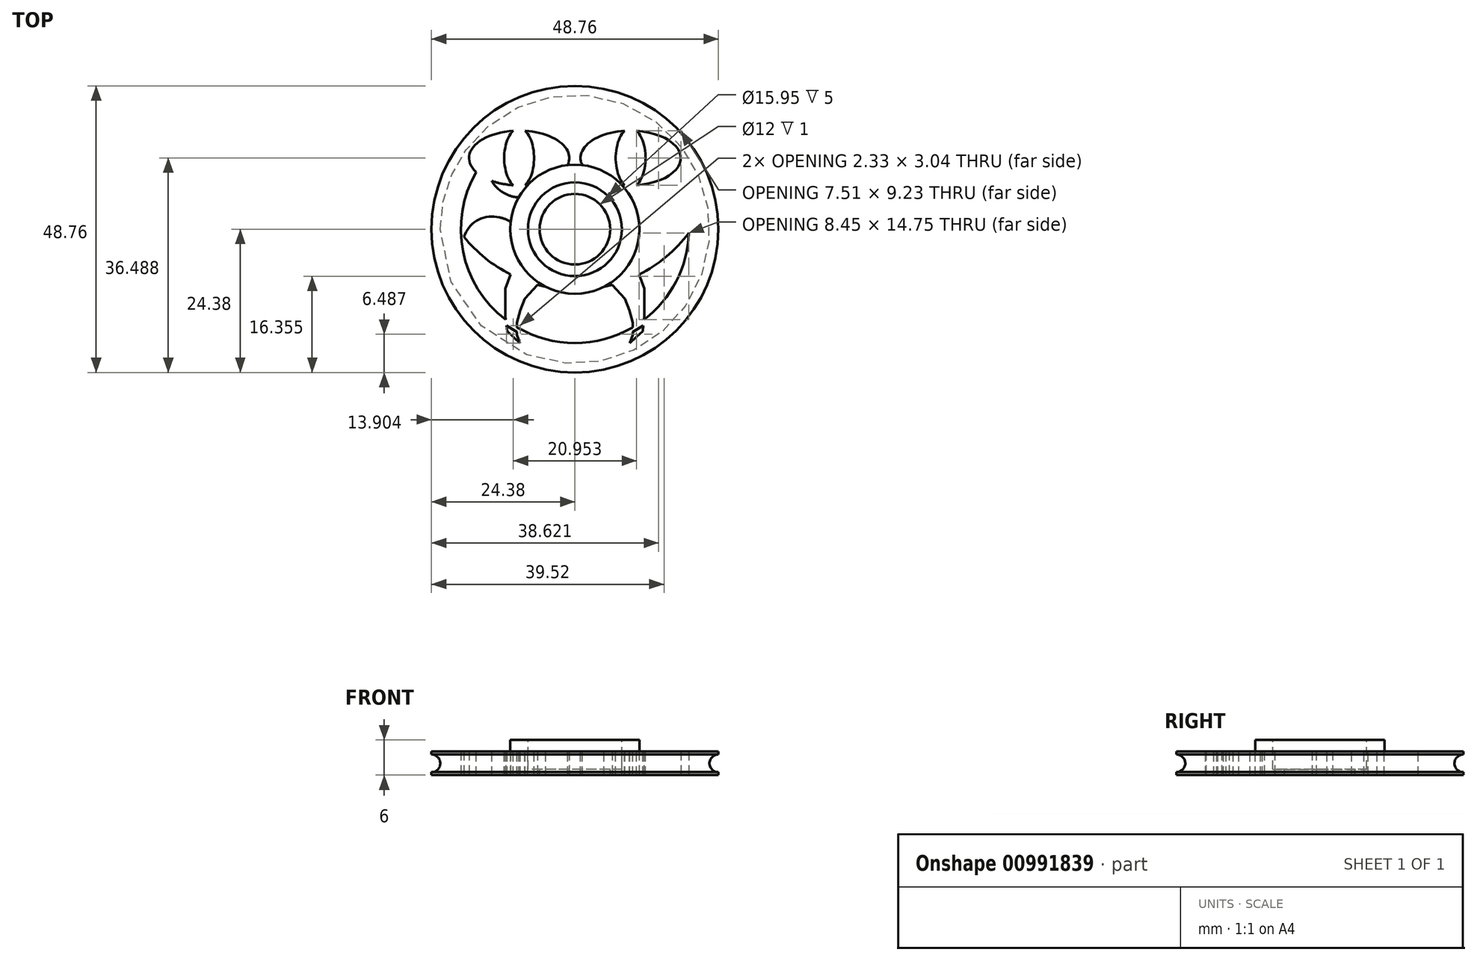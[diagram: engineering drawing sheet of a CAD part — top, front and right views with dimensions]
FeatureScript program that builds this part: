
annotation { "Feature Type Name" : "Feature", "Feature Type Description" : "" }
export const myFeature = defineFeature(function(context is Context, id is Id, definition is map)
    precondition{}
    {
        {
            var Q0;
            Q0=qCreatedBy(makeId("Top.planeOp"),FACE);
            var sketch = newSketch(context, id + "F0", { "sketchPlane" : qUnion([Q0])});
            skCircle(sketch, "E0", {"center": v(0, 0) * mm, "radius": 24.38 * mm});
            skCircle(sketch, "E1", {"center": v(0, 0) * mm, "radius": 8 * mm});
            skArc(sketch, "E2", {"start": v(-4.5, 7.8) * mm, "mid": v(0, -9) * mm, "end": v(4.5, 7.8) * mm});
            skArc(sketch, "E3.0", {"start": v(-9.52, 16.88) * mm, "mid": v(0, -19.38) * mm, "end": v(9.52, 16.88) * mm});
            skLineSegment(sketch, "E4.0", {"start": v(-2.12, 13.29) * mm, "end": v(-2.06, 12.89) * mm});
            skLineSegment(sketch, "E5.0", {"start": v(2.12, 13.29) * mm, "end": v(2.06, 12.89) * mm});
            skPoint(sketch, "E6.orphan", {"position": v(0, 21.65) * mm});
            skPoint(sketch, "E7.visualSharp", {"position": v(-1.44, 8.88) * mm});
            skArc(sketch, "E7.filletArc", {"start": v(-4.5, 7.8) * mm, "mid": v(-2.5, 9.96) * mm, "end": v(-2.06, 12.89) * mm});
            skPoint(sketch, "E8.visualSharp", {"position": v(1.44, 8.88) * mm});
            skArc(sketch, "E8.filletArc", {"start": v(2.06, 12.89) * mm, "mid": v(2.5, 9.96) * mm, "end": v(4.5, 7.8) * mm});
            skPoint(sketch, "E9.visualSharp", {"position": v(3.03, 19.14) * mm});
            skArc(sketch, "E9.filletArc", {"start": v(9.52, 16.88) * mm, "mid": v(4.88, 17.02) * mm, "end": v(2.12, 13.29) * mm});
            skPoint(sketch, "E10.visualSharp", {"position": v(-3.03, 19.14) * mm});
            skArc(sketch, "E10.filletArc", {"start": v(-2.12, 13.29) * mm, "mid": v(-4.88, 17.02) * mm, "end": v(-9.52, 16.88) * mm});
            skArc(sketch, "E11.1.0", {"start": v(-13.3, 2.09) * mm, "mid": v(-17.7, 0.62) * mm, "end": v(-19, -3.84) * mm});
            skLineSegment(sketch, "E11.1.1", {"start": v(-13.3, 2.09) * mm, "end": v(-12.9, 2.02) * mm});
            skArc(sketch, "E11.1.2", {"start": v(-8.8, -1.87) * mm, "mid": v(-10.25, 0.71) * mm, "end": v(-12.9, 2.02) * mm});
            skArc(sketch, "E11.1.3", {"start": v(-11.62, 5.94) * mm, "mid": v(-8.7, 5.45) * mm, "end": v(-6.02, 6.69) * mm});
            skLineSegment(sketch, "E11.1.4", {"start": v(-11.98, 6.12) * mm, "end": v(-11.62, 5.94) * mm});
            skArc(sketch, "E11.1.5", {"start": v(-13.1, 14.27) * mm, "mid": v(-14.68, 9.9) * mm, "end": v(-11.98, 6.12) * mm});
            skArc(sketch, "E11.2.0", {"start": v(-6.1, -12) * mm, "mid": v(-6.06, -16.64) * mm, "end": v(-2.22, -19.25) * mm});
            skLineSegment(sketch, "E11.2.1", {"start": v(-6.1, -12) * mm, "end": v(-5.91, -11.64) * mm});
            skArc(sketch, "E11.2.2", {"start": v(-0.94, -8.95) * mm, "mid": v(-3.84, -9.53) * mm, "end": v(-5.91, -11.64) * mm});
            skArc(sketch, "E11.2.3", {"start": v(-9.24, -9.22) * mm, "mid": v(-7.87, -6.6) * mm, "end": v(-8.22, -3.66) * mm});
            skLineSegment(sketch, "E11.2.4", {"start": v(-9.52, -9.5) * mm, "end": v(-9.24, -9.22) * mm});
            skArc(sketch, "E11.2.5", {"start": v(-17.62, -8.06) * mm, "mid": v(-13.95, -10.9) * mm, "end": v(-9.52, -9.5) * mm});
            skArc(sketch, "E11.3.0", {"start": v(9.52, -9.5) * mm, "mid": v(13.95, -10.9) * mm, "end": v(17.62, -8.06) * mm});
            skLineSegment(sketch, "E11.3.1", {"start": v(9.52, -9.5) * mm, "end": v(9.24, -9.22) * mm});
            skArc(sketch, "E11.3.2", {"start": v(8.22, -3.66) * mm, "mid": v(7.87, -6.6) * mm, "end": v(9.24, -9.22) * mm});
            skArc(sketch, "E11.3.3", {"start": v(5.91, -11.64) * mm, "mid": v(3.84, -9.53) * mm, "end": v(0.94, -8.95) * mm});
            skLineSegment(sketch, "E11.3.4", {"start": v(6.1, -12) * mm, "end": v(5.91, -11.64) * mm});
            skArc(sketch, "E11.3.5", {"start": v(2.22, -19.25) * mm, "mid": v(6.06, -16.64) * mm, "end": v(6.1, -12) * mm});
            skArc(sketch, "E11.4.0", {"start": v(11.98, 6.12) * mm, "mid": v(14.68, 9.9) * mm, "end": v(13.1, 14.27) * mm});
            skLineSegment(sketch, "E11.4.1", {"start": v(11.98, 6.12) * mm, "end": v(11.62, 5.94) * mm});
            skArc(sketch, "E11.4.2", {"start": v(6.02, 6.69) * mm, "mid": v(8.7, 5.45) * mm, "end": v(11.62, 5.94) * mm});
            skArc(sketch, "E11.4.3", {"start": v(12.9, 2.02) * mm, "mid": v(10.25, 0.71) * mm, "end": v(8.8, -1.87) * mm});
            skLineSegment(sketch, "E11.4.4", {"start": v(13.3, 2.09) * mm, "end": v(12.9, 2.02) * mm});
            skArc(sketch, "E11.4.5", {"start": v(19, -3.84) * mm, "mid": v(17.7, 0.62) * mm, "end": v(13.3, 2.09) * mm});
            skCircle(sketch, "E12", {"center": v(0, 13.95) * mm, "radius": 24.25 * mm});
            skSolve(sketch);
        }
        {
            var Q0;
            Q0=makeQuery(id+"F0.imprint","IMPRINT",FACE,{"disambiguationData":[TD([[makeQuery(id+"F0.imprint","IMPRINT",EDGE,{"derivedFrom":sQuery(id+"F0.wireOp",EDGE,"E0")}),1.0]])]});
            var Q1;
            {var subQ0=sQuery(id+"F0.wireOp",EDGE,"E11.4.0");Q1=makeQuery(id+"F0.imprint","IMPRINT",FACE,{"disambiguationData":[TD([[makeQuery(id+"F0.imprint","IMPRINT",EDGE,{"derivedFrom":subQ0}),-1.0]])]});}
            var Q2;
            Q2=makeQuery(id+"F0.imprint","IMPRINT",FACE,{"disambiguationData":[TD([[makeQuery(id+"F0.imprint","IMPRINT",EDGE,{"derivedFrom":sQuery(id+"F0.wireOp",EDGE,"E1")}),-1.0]])]});
            var Q3;
            {var subQ0=sQuery(id+"F0.wireOp",EDGE,"E11.1.1");Q3=makeQuery(id+"F0.imprint","IMPRINT",FACE,{"disambiguationData":[TD([[makeQuery(id+"F0.imprint","IMPRINT",EDGE,{"derivedFrom":subQ0}),1.0]])]});}
            var Q4;
            {var subQ1=sQuery(id+"F0.wireOp",EDGE,"E11.2.3");Q4=makeQuery(id+"F0.imprint","IMPRINT",FACE,{"disambiguationData":[TD([[makeQuery(id+"F0.imprint","IMPRINT",EDGE,{"derivedFrom":subQ1}),-1.0]])]});}
            var Q5;
            {var subQ5=sQuery(id+"F0.wireOp",EDGE,"E11.3.2");Q5=makeQuery(id+"F0.imprint","IMPRINT",FACE,{"disambiguationData":[TD([[makeQuery(id+"F0.imprint","IMPRINT",EDGE,{"derivedFrom":subQ5}),-1.0]])]});}
            var Q6;
            {var subQ1=sQuery(id+"F0.wireOp",EDGE,"E11.1.1");Q6=makeQuery(id+"F0.imprint","IMPRINT",FACE,{"disambiguationData":[TD([[makeQuery(id+"F0.imprint","IMPRINT",EDGE,{"derivedFrom":subQ1}),-1.0]])]});}
            var Q7;
            {var subQ0=sQuery(id+"F0.wireOp",EDGE,"E11.2.2");var subQ1=sQuery(id+"F0.wireOp",EDGE,"E2");var subQ2=makeQuery(id+"F0.imprint","INTERSECT",VERTEX,{"derivedFrom":[subQ1,subQ0]});Q7=makeQuery(id+"F0.imprint","IMPRINT",FACE,{"disambiguationData":[TD([[makeQuery(id+"F0.imprint","IMPRINT",EDGE,{"disambiguationData":[TD([[subQ2,-1.0]])],"derivedFrom":subQ1}),-1.0]])]});}
            var Q8;
            {var subQ0=sQuery(id+"F0.wireOp",EDGE,"E11.4.3");Q8=makeQuery(id+"F0.imprint","IMPRINT",FACE,{"disambiguationData":[TD([[makeQuery(id+"F0.imprint","IMPRINT",EDGE,{"derivedFrom":subQ0}),1.0]])]});}
            extrude(context, id + "F1", {"entities" : qUnion([Q0, Q1, Q2, Q3, Q4, Q5, Q6, Q7, Q8]), "depth" : 4 * mm, "offsetDistance" : 25.4 * mm, "symmetric" : true});
        }
        {
            var Q0;
            Q0=qCreatedBy(makeId("Top.planeOp"),FACE);
            var sketch = newSketch(context, id + "F2", { "sketchPlane" : qUnion([Q0])});
            skLineSegment(sketch, "E13", {"start": v(-14.44, -5.48) * mm, "end": v(-16.84, -9.61) * mm});
            skLineSegment(sketch, "E14", {"start": v(-16.84, -9.61) * mm, "end": v(-15.72, -11.69) * mm});
            skLineSegment(sketch, "E15", {"start": v(-15.72, -11.69) * mm, "end": v(-12.24, -6.68) * mm});
            skLineSegment(sketch, "E16", {"start": v(-12.24, -6.68) * mm, "end": v(-9.08, -8.27) * mm});
            skLineSegment(sketch, "E17", {"start": v(-9.08, -8.27) * mm, "end": v(-12.78, -12.6) * mm});
            skLineSegment(sketch, "E18", {"start": v(-12.78, -12.6) * mm, "end": v(-13.23, -11.08) * mm});
            skLineSegment(sketch, "E19", {"start": v(-13.23, -11.08) * mm, "end": v(-14.16, -11.08) * mm});
            skLineSegment(sketch, "E20", {"start": v(-14.16, -11.08) * mm, "end": v(-14.82, -11.08) * mm});
            skLineSegment(sketch, "E21", {"start": v(-14.82, -11.08) * mm, "end": v(-15.14, -10.86) * mm});
            skLineSegment(sketch, "E22", {"start": v(-4.98, -9.03) * mm, "end": v(-8.45, -15.68) * mm});
            skLineSegment(sketch, "E23", {"start": v(-1.8, -17.1) * mm, "end": v(-0.72, -9.57) * mm});
            skLineSegment(sketch, "E24", {"start": v(0.8, -9.78) * mm, "end": v(1.77, -17.83) * mm});
            skLineSegment(sketch, "E25", {"start": v(6.47, -15.97) * mm, "end": v(4.75, -8.64) * mm});
            skLineSegment(sketch, "E26", {"start": v(-8.6, -8.27) * mm, "end": v(-13.47, -13.99) * mm});
            skLineSegment(sketch, "E27", {"start": v(-13.47, -13.99) * mm, "end": v(-12.24, -13.99) * mm});
            skLineSegment(sketch, "E28", {"start": v(-12.24, -13.99) * mm, "end": v(-11.5, -14.36) * mm});
            skLineSegment(sketch, "E29", {"start": v(-11.5, -14.36) * mm, "end": v(-11.43, -15.48) * mm});
            skLineSegment(sketch, "E30", {"start": v(-11.43, -15.48) * mm, "end": v(-11, -16.02) * mm});
            skLineSegment(sketch, "E31", {"start": v(-11, -16.02) * mm, "end": v(-10.2, -16.27) * mm});
            skLineSegment(sketch, "E32", {"start": v(-10.2, -16.27) * mm, "end": v(-7.92, -13.58) * mm});
            skLineSegment(sketch, "E33", {"start": v(-7.92, -13.58) * mm, "end": v(-6.92, -11.6) * mm});
            skLineSegment(sketch, "E34", {"start": v(-6.92, -11.6) * mm, "end": v(-6.1, -8.93) * mm});
            skLineSegment(sketch, "E35", {"start": v(5.83, -9.57) * mm, "end": v(6.89, -14.1) * mm});
            skLineSegment(sketch, "E36", {"start": v(6.89, -14.1) * mm, "end": v(11.16, -12.01) * mm});
            skLineSegment(sketch, "E37", {"start": v(11.16, -12.01) * mm, "end": v(10.22, -7.97) * mm});
            skLineSegment(sketch, "E38", {"start": v(10.22, -7.97) * mm, "end": v(13.16, -14.55) * mm});
            skLineSegment(sketch, "E39", {"start": v(13.16, -14.55) * mm, "end": v(14.29, -13.09) * mm});
            skLineSegment(sketch, "E40", {"start": v(14.29, -13.09) * mm, "end": v(15.36, -10.64) * mm});
            skLineSegment(sketch, "E41", {"start": v(15.36, -10.64) * mm, "end": v(14.11, -10.46) * mm});
            skLineSegment(sketch, "E42", {"start": v(14.11, -10.46) * mm, "end": v(13.16, -9.57) * mm});
            skLineSegment(sketch, "E43", {"start": v(13.16, -9.57) * mm, "end": v(13.16, -7.95) * mm});
            skLineSegment(sketch, "E44", {"start": v(13.16, -7.95) * mm, "end": v(13.02, -6.39) * mm});
            skLineSegment(sketch, "E45", {"start": v(-14.44, -5.48) * mm, "end": v(-12.24, -6.68) * mm});
            skLineSegment(sketch, "E46", {"start": v(-8.6, -8.27) * mm, "end": v(-6.1, -8.93) * mm});
            skLineSegment(sketch, "E47", {"start": v(-4.98, -9.03) * mm, "end": v(-0.72, -9.57) * mm});
            skLineSegment(sketch, "E48", {"start": v(0.8, -9.78) * mm, "end": v(4.75, -8.64) * mm});
            skLineSegment(sketch, "E49", {"start": v(5.83, -9.57) * mm, "end": v(10.22, -7.97) * mm});
            skLineSegment(sketch, "E50", {"start": v(10.22, -7.97) * mm, "end": v(13.02, -6.39) * mm});
            skLineSegment(sketch, "E51", {"start": v(13.52, -5.97) * mm, "end": v(14.5, -8.94) * mm});
            skLineSegment(sketch, "E52", {"start": v(14.5, -8.94) * mm, "end": v(15.67, -8.94) * mm});
            skLineSegment(sketch, "E53", {"start": v(15.67, -8.94) * mm, "end": v(16.95, -8.28) * mm});
            skLineSegment(sketch, "E54", {"start": v(16.95, -8.28) * mm, "end": v(17.81, -7.9) * mm});
            skLineSegment(sketch, "E55", {"start": v(17.81, -7.9) * mm, "end": v(18.02, -7.07) * mm});
            skLineSegment(sketch, "E56", {"start": v(18.02, -7.07) * mm, "end": v(17.67, -6.3) * mm});
            skLineSegment(sketch, "E57", {"start": v(17.67, -6.3) * mm, "end": v(17.06, -4.94) * mm});
            skLineSegment(sketch, "E58", {"start": v(17.06, -4.94) * mm, "end": v(16.19, -3.72) * mm});
            skLineSegment(sketch, "E59", {"start": v(16.19, -3.72) * mm, "end": v(13.52, -5.97) * mm});
            skLineSegment(sketch, "E60", {"start": v(-8.45, -15.68) * mm, "end": v(-6.08, -16.91) * mm});
            skLineSegment(sketch, "E61", {"start": v(-6.08, -16.91) * mm, "end": v(-4.84, -18.74) * mm});
            skLineSegment(sketch, "E62", {"start": v(-4.84, -18.74) * mm, "end": v(-3.33, -19.9) * mm});
            skLineSegment(sketch, "E63", {"start": v(-3.33, -19.9) * mm, "end": v(-1.8, -17.1) * mm});
            skLineSegment(sketch, "E64", {"start": v(11.16, -12.01) * mm, "end": v(11.88, -11.69) * mm});
            skLineSegment(sketch, "E65", {"start": v(1.77, -17.83) * mm, "end": v(3.1, -17.67) * mm});
            skLineSegment(sketch, "E66", {"start": v(3.1, -17.67) * mm, "end": v(3.94, -18.9) * mm});
            skLineSegment(sketch, "E67", {"start": v(3.94, -18.9) * mm, "end": v(5.39, -18.9) * mm});
            skLineSegment(sketch, "E68", {"start": v(5.39, -18.9) * mm, "end": v(5.39, -17.83) * mm});
            skLineSegment(sketch, "E69", {"start": v(5.84, -13.31) * mm, "end": v(6.47, -15.97) * mm});
            skLineSegment(sketch, "E70", {"start": v(5.39, -17.83) * mm, "end": v(6.5, -17.3) * mm});
            skLineSegment(sketch, "E71", {"start": v(6.5, -17.3) * mm, "end": v(6.47, -15.97) * mm});
            skSolve(sketch);
        }
        {
            var Q0;
            Q0=qCreatedBy(makeId("Top.planeOp"),FACE);
            var sketch = newSketch(context, id + "F3", { "sketchPlane" : qUnion([Q0])});
            skEllipse(sketch, "E72", {"center": v(-9.48, 12.1) * mm, "majorRadius": 8.52 * mm, "minorRadius": 4.65 * mm, "majorAxis": v(-1, 0)});
            skEllipse(sketch, "E73.MirrorC", {"center": v(9.48, 12.1) * mm, "majorRadius": 8.52 * mm, "minorRadius": 4.65 * mm, "majorAxis": v(1, 0)});
            skSolve(sketch);
        }
        {
            var Q0;
            Q0=makeQuery(id+"F0.imprint","IMPRINT",FACE,{"disambiguationData":[TD([[makeQuery(id+"F0.imprint","IMPRINT",EDGE,{"derivedFrom":sQuery(id+"F0.wireOp",EDGE,"E1")}),-1.0]])]});
            var Q1;
            {var subQ0=sQuery(id+"F0.wireOp",EDGE,"E11.1.1");Q1=makeQuery(id+"F0.imprint","IMPRINT",FACE,{"disambiguationData":[TD([[makeQuery(id+"F0.imprint","IMPRINT",EDGE,{"derivedFrom":subQ0}),1.0]])]});}
            var Q2;
            {var subQ0=sQuery(id+"F0.wireOp",EDGE,"E11.4.0");Q2=makeQuery(id+"F0.imprint","IMPRINT",FACE,{"disambiguationData":[TD([[makeQuery(id+"F0.imprint","IMPRINT",EDGE,{"derivedFrom":subQ0}),-1.0]])]});}
            var Q3;
            Q3=makeQuery(id+"F0.imprint","IMPRINT",FACE,{"disambiguationData":[TD([[makeQuery(id+"F0.imprint","IMPRINT",EDGE,{"derivedFrom":sQuery(id+"F0.wireOp",EDGE,"E5.0")}),1.0]])]});
            var Q4;
            Q4=makeQuery(id+"F0.imprint","IMPRINT",FACE,{"disambiguationData":[TD([[makeQuery(id+"F0.imprint","IMPRINT",EDGE,{"derivedFrom":sQuery(id+"F0.wireOp",EDGE,"E4.0")}),-1.0]])]});
            extrude(context, id + "F4", {"entities" : qUnion([Q0, Q1, Q2, Q3, Q4]), "operationType" : NewBodyOperationType.ADD, "depth" : 4 * mm, "offsetDistance" : 25.4 * mm, "symmetric" : true});
        }
        {
            var Q0;
            Q0=qSketchRegion(id+"F3",true);
            extrude(context, id + "F5", {"entities" : qUnion([Q0]), "operationType" : NewBodyOperationType.REMOVE, "oppositeDirection" : true, "depth" : 5 * mm, "offsetDistance" : 25.4 * mm, "symmetric" : true});
        }
        {
            var Q0;
            {var subQ0=sQuery(id+"F0.wireOp",EDGE,"E12");var subQ1=sQuery(id+"F0.wireOp",EDGE,"E11.1.0");var subQ2=sQuery(id+"F0.wireOp",EDGE,"E2");var subQ3=sQuery(id+"F0.wireOp",EDGE,"E1");var subQ4=sQuery(id+"F0.wireOp",EDGE,"E0");Q0=makeQuery(id+"F4.boolean.opBoolean","MERGE",FACE,{"derivedFrom":[makeQuery(id+"F1.opExtrude","CAP_FACE",FACE,{"disambiguationData":[OSD([subQ4,subQ3,subQ2,sQuery(id+"F0.wireOp",EDGE,"E3.0"),sQuery(id+"F0.wireOp",EDGE,"E4.0"),sQuery(id+"F0.wireOp",EDGE,"E5.0"),sQuery(id+"F0.wireOp",EDGE,"E7.filletArc"),sQuery(id+"F0.wireOp",EDGE,"E8.filletArc"),sQuery(id+"F0.wireOp",EDGE,"E9.filletArc"),sQuery(id+"F0.wireOp",EDGE,"E10.filletArc"),subQ1,sQuery(id+"F0.wireOp",EDGE,"E11.1.3"),sQuery(id+"F0.wireOp",EDGE,"E11.1.4"),sQuery(id+"F0.wireOp",EDGE,"E11.1.5"),sQuery(id+"F0.wireOp",EDGE,"E11.4.0"),sQuery(id+"F0.wireOp",EDGE,"E11.4.1"),sQuery(id+"F0.wireOp",EDGE,"E11.4.2"),subQ0])],"isStart":false}),makeQuery(id+"F4.opExtrude","CAP_FACE",FACE,{"disambiguationData":[OSD([subQ4,subQ3,subQ2,subQ1,sQuery(id+"F0.wireOp",EDGE,"E11.1.1"),sQuery(id+"F0.wireOp",EDGE,"E11.1.2"),sQuery(id+"F0.wireOp",EDGE,"E11.4.3"),sQuery(id+"F0.wireOp",EDGE,"E11.4.4"),sQuery(id+"F0.wireOp",EDGE,"E11.4.5"),subQ0])],"isStart":false})]});}
            var sketch = newSketch(context, id + "F6", { "sketchPlane" : qUnion([Q0])});
            skLineSegment(sketch, "E74", {"start": v(-10.73, -7.2) * mm, "end": v(-11.83, -10.11) * mm});
            skLineSegment(sketch, "E75", {"start": v(-11.83, -10.11) * mm, "end": v(-11.83, -13.22) * mm});
            skLineSegment(sketch, "E76", {"start": v(-11.83, -13.22) * mm, "end": v(-11.83, -14.74) * mm});
            skLineSegment(sketch, "E77", {"start": v(-11.83, -14.74) * mm, "end": v(-11.21, -16.75) * mm});
            skLineSegment(sketch, "E78", {"start": v(-11.21, -16.75) * mm, "end": v(-9.83, -18) * mm});
            skLineSegment(sketch, "E79", {"start": v(-9.83, -18) * mm, "end": v(-9.83, -15.92) * mm});
            skLineSegment(sketch, "E80", {"start": v(-9.83, -15.92) * mm, "end": v(-9.28, -13.78) * mm});
            skLineSegment(sketch, "E81", {"start": v(-9.28, -13.78) * mm, "end": v(-8.51, -11.84) * mm});
            skLineSegment(sketch, "E82", {"start": v(-8.51, -11.84) * mm, "end": v(-7.06, -10.22) * mm});
            skLineSegment(sketch, "E83", {"start": v(-7.06, -10.22) * mm, "end": v(-6.26, -9.33) * mm});
            skLineSegment(sketch, "E84", {"start": v(-6.26, -9.33) * mm, "end": v(-5.61, -7.98) * mm});
            skLineSegment(sketch, "E85", {"start": v(-5.61, -7.98) * mm, "end": v(-9.83, -5.47) * mm});
            skLineSegment(sketch, "E86", {"start": v(-9.83, -5.47) * mm, "end": v(-10.73, -7.2) * mm});
            skLineSegment(sketch, "E87", {"start": v(-11.83, -14.74) * mm, "end": v(-11.52, -17.36) * mm});
            skPoint(sketch, "E87.endSnap0", {"position": v(-11.52, -15.75) * mm});
            skLineSegment(sketch, "E88", {"start": v(-11.52, -17.36) * mm, "end": v(-10.42, -18.39) * mm});
            skLineSegment(sketch, "E89", {"start": v(-10.42, -18.39) * mm, "end": v(-9.31, -19.41) * mm});
            skLineSegment(sketch, "E90", {"start": v(-9.31, -19.41) * mm, "end": v(-9.83, -18) * mm});
            skLineSegment(sketch, "E91", {"start": v(-9.83, -17.52) * mm, "end": v(-11.6, -16.66) * mm});
            skLineSegment(sketch, "E92", {"start": v(-9.83, -16.96) * mm, "end": v(-11.71, -15.78) * mm});
            skLineSegment(sketch, "E93.MirrorCS", {"start": v(5.61, -7.98) * mm, "end": v(9.83, -5.47) * mm});
            skLineSegment(sketch, "E94.MirrorCS", {"start": v(9.83, -5.47) * mm, "end": v(10.73, -7.2) * mm});
            skLineSegment(sketch, "E95.MirrorCS", {"start": v(10.73, -7.2) * mm, "end": v(11.83, -10.11) * mm});
            skLineSegment(sketch, "E96.MirrorCS", {"start": v(11.83, -10.11) * mm, "end": v(11.83, -13.22) * mm});
            skLineSegment(sketch, "E97.MirrorCS", {"start": v(11.83, -13.22) * mm, "end": v(11.83, -14.74) * mm});
            skLineSegment(sketch, "E98.MirrorCS", {"start": v(11.83, -14.74) * mm, "end": v(11.52, -17.36) * mm});
            skLineSegment(sketch, "E99.MirrorCS", {"start": v(11.52, -17.36) * mm, "end": v(10.42, -18.39) * mm});
            skLineSegment(sketch, "E100.MirrorCS", {"start": v(10.42, -18.39) * mm, "end": v(9.31, -19.41) * mm});
            skLineSegment(sketch, "E101.MirrorCS", {"start": v(9.31, -19.41) * mm, "end": v(9.83, -18) * mm});
            skLineSegment(sketch, "E102.MirrorCS", {"start": v(9.83, -15.92) * mm, "end": v(9.28, -13.78) * mm});
            skLineSegment(sketch, "E103.MirrorCS", {"start": v(9.28, -13.78) * mm, "end": v(8.51, -11.84) * mm});
            skLineSegment(sketch, "E104.MirrorCS", {"start": v(8.51, -11.84) * mm, "end": v(7.06, -10.22) * mm});
            skLineSegment(sketch, "E105.MirrorCS", {"start": v(7.06, -10.22) * mm, "end": v(6.26, -9.33) * mm});
            skLineSegment(sketch, "E106.MirrorCS", {"start": v(6.26, -9.33) * mm, "end": v(5.61, -7.98) * mm});
            skLineSegment(sketch, "E107.MirrorCS", {"start": v(9.83, -18) * mm, "end": v(9.83, -15.92) * mm});
            skLineSegment(sketch, "E108.MirrorCS", {"start": v(9.83, -16.96) * mm, "end": v(11.71, -15.78) * mm});
            skLineSegment(sketch, "E109.MirrorCS", {"start": v(11.21, -16.75) * mm, "end": v(9.83, -18) * mm});
            skLineSegment(sketch, "E110.MirrorCS", {"start": v(9.83, -17.52) * mm, "end": v(11.6, -16.66) * mm});
            skSolve(sketch);
        }
        {
            var Q0;
            Q0=qSketchRegion(id+"F6",true);
            extrude(context, id + "F7", {"entities" : qUnion([Q0]), "operationType" : NewBodyOperationType.ADD, "oppositeDirection" : true, "depth" : 4 * mm, "offsetDistance" : 25.4 * mm});
        }
        {
            var Q0;
            {var subQ3=sQuery(id+"F6.wireOp",EDGE,"E78");var subQ5=sQuery(id+"F6.wireOp",EDGE,"E77");var subQ6=makeQuery(id+"F6.imprint","INTERSECT",VERTEX,{"derivedFrom":[subQ5,subQ3]});Q0=makeQuery(id+"F6.imprint","IMPRINT",FACE,{"disambiguationData":[TD([[makeQuery(id+"F6.imprint","IMPRINT",EDGE,{"disambiguationData":[TD([[subQ6,1.0]])],"derivedFrom":subQ5}),-1.0]])]});}
            var Q1;
            {var subQ3=sQuery(id+"F6.wireOp",EDGE,"E78");var subQ5=sQuery(id+"F6.wireOp",EDGE,"E77");var subQ6=makeQuery(id+"F6.imprint","INTERSECT",VERTEX,{"derivedFrom":[subQ5,subQ3]});Q1=makeQuery(id+"F6.imprint","IMPRINT",FACE,{"disambiguationData":[TD([[makeQuery(id+"F6.imprint","IMPRINT",EDGE,{"disambiguationData":[TD([[subQ6,1.0]])],"derivedFrom":subQ5}),1.0]])]});}
            var Q2;
            {var subQ0=sQuery(id+"F6.wireOp",EDGE,"E79");var subQ3=sQuery(id+"F6.wireOp",EDGE,"E91");var subQ5=makeQuery(id+"F6.imprint","INTERSECT",VERTEX,{"derivedFrom":[subQ0,subQ3]});Q2=makeQuery(id+"F6.imprint","IMPRINT",FACE,{"disambiguationData":[TD([[makeQuery(id+"F6.imprint","IMPRINT",EDGE,{"disambiguationData":[TD([[subQ5,-1.0]])],"derivedFrom":subQ3}),1.0]])]});}
            var Q3;
            {var subQ0=sQuery(id+"F6.wireOp",EDGE,"E88");Q3=makeQuery(id+"F6.imprint","IMPRINT",FACE,{"disambiguationData":[TD([[makeQuery(id+"F6.imprint","IMPRINT",EDGE,{"derivedFrom":subQ0}),1.0]])]});}
            var Q4;
            {var subQ1=sQuery(id+"F6.wireOp",EDGE,"E107.MirrorCS");var subQ3=sQuery(id+"F6.wireOp",EDGE,"E110.MirrorCS");var subQ4=makeQuery(id+"F6.imprint","INTERSECT",VERTEX,{"derivedFrom":[subQ1,subQ3]});Q4=makeQuery(id+"F6.imprint","IMPRINT",FACE,{"disambiguationData":[TD([[makeQuery(id+"F6.imprint","IMPRINT",EDGE,{"disambiguationData":[TD([[subQ4,-1.0]])],"derivedFrom":subQ3}),-1.0]])]});}
            var Q5;
            {var subQ1=sQuery(id+"F6.wireOp",EDGE,"E99.MirrorCS");Q5=makeQuery(id+"F6.imprint","IMPRINT",FACE,{"disambiguationData":[TD([[makeQuery(id+"F6.imprint","IMPRINT",EDGE,{"derivedFrom":subQ1}),-1.0]])]});}
            var Q6;
            {var subQ4=sQuery(id+"F6.wireOp",EDGE,"E108.MirrorCS");Q6=makeQuery(id+"F6.imprint","IMPRINT",FACE,{"disambiguationData":[TD([[makeQuery(id+"F6.imprint","IMPRINT",EDGE,{"derivedFrom":subQ4}),-1.0]])]});}
            extrude(context, id + "F8", {"entities" : qUnion([Q0, Q1, Q2, Q3, Q4, Q5, Q6]), "operationType" : NewBodyOperationType.REMOVE, "oppositeDirection" : true, "depth" : 25.4 * mm, "offsetDistance" : 25.4 * mm});
        }
        {
            var Q0;
            Q0=qCreatedBy(makeId("Front.planeOp"),FACE);
            var sketch = newSketch(context, id + "F9", { "sketchPlane" : qUnion([Q0])});
            skCircle(sketch, "E111", {"center": v(-24.38, 0) * mm, "radius": 1.5 * mm});
            skLineSegment(sketch, "E112", {"start": v(0, 3.3) * mm, "end": v(0, -4.33) * mm, "construction": true});
            skSolve(sketch);
        }
        {
            var Q0;
            {var subQ0=sQuery(id+"F0.wireOp",EDGE,"E12");var subQ1=sQuery(id+"F0.wireOp",EDGE,"E11.1.0");var subQ2=sQuery(id+"F0.wireOp",EDGE,"E2");var subQ3=sQuery(id+"F0.wireOp",EDGE,"E1");var subQ4=sQuery(id+"F0.wireOp",EDGE,"E0");Q0=makeQuery(id+"F7.boolean.opBoolean","MERGE",FACE,{"derivedFrom":[makeQuery(id+"F4.boolean.opBoolean","MERGE",FACE,{"derivedFrom":[makeQuery(id+"F1.opExtrude","CAP_FACE",FACE,{"disambiguationData":[OSD([subQ4,subQ3,subQ2,sQuery(id+"F0.wireOp",EDGE,"E3.0"),sQuery(id+"F0.wireOp",EDGE,"E4.0"),sQuery(id+"F0.wireOp",EDGE,"E5.0"),sQuery(id+"F0.wireOp",EDGE,"E7.filletArc"),sQuery(id+"F0.wireOp",EDGE,"E8.filletArc"),sQuery(id+"F0.wireOp",EDGE,"E9.filletArc"),sQuery(id+"F0.wireOp",EDGE,"E10.filletArc"),subQ1,sQuery(id+"F0.wireOp",EDGE,"E11.1.3"),sQuery(id+"F0.wireOp",EDGE,"E11.1.4"),sQuery(id+"F0.wireOp",EDGE,"E11.1.5"),sQuery(id+"F0.wireOp",EDGE,"E11.4.0"),sQuery(id+"F0.wireOp",EDGE,"E11.4.1"),sQuery(id+"F0.wireOp",EDGE,"E11.4.2"),subQ0])],"isStart":false}),makeQuery(id+"F4.opExtrude","CAP_FACE",FACE,{"disambiguationData":[OSD([subQ4,subQ3,subQ2,subQ1,sQuery(id+"F0.wireOp",EDGE,"E11.1.1"),sQuery(id+"F0.wireOp",EDGE,"E11.1.2"),sQuery(id+"F0.wireOp",EDGE,"E11.4.3"),sQuery(id+"F0.wireOp",EDGE,"E11.4.4"),sQuery(id+"F0.wireOp",EDGE,"E11.4.5"),subQ0])],"isStart":false})]}),makeQuery(id+"F7.opExtrude","CAP_FACE",FACE,{"disambiguationData":[OSD([sQuery(id+"F6.wireOp",EDGE,"E74"),sQuery(id+"F6.wireOp",EDGE,"E75"),sQuery(id+"F6.wireOp",EDGE,"E76"),sQuery(id+"F6.wireOp",EDGE,"E79"),sQuery(id+"F6.wireOp",EDGE,"E80"),sQuery(id+"F6.wireOp",EDGE,"E81"),sQuery(id+"F6.wireOp",EDGE,"E82"),sQuery(id+"F6.wireOp",EDGE,"E83"),sQuery(id+"F6.wireOp",EDGE,"E84"),sQuery(id+"F6.wireOp",EDGE,"E85"),sQuery(id+"F6.wireOp",EDGE,"E86"),sQuery(id+"F6.wireOp",EDGE,"E87"),sQuery(id+"F6.wireOp",EDGE,"E88"),sQuery(id+"F6.wireOp",EDGE,"E89"),sQuery(id+"F6.wireOp",EDGE,"E90")])],"isStart":true}),makeQuery(id+"F7.opExtrude","CAP_FACE",FACE,{"disambiguationData":[OSD([sQuery(id+"F6.wireOp",EDGE,"E93.MirrorCS"),sQuery(id+"F6.wireOp",EDGE,"E94.MirrorCS"),sQuery(id+"F6.wireOp",EDGE,"E95.MirrorCS"),sQuery(id+"F6.wireOp",EDGE,"E96.MirrorCS"),sQuery(id+"F6.wireOp",EDGE,"E97.MirrorCS"),sQuery(id+"F6.wireOp",EDGE,"E98.MirrorCS"),sQuery(id+"F6.wireOp",EDGE,"E99.MirrorCS"),sQuery(id+"F6.wireOp",EDGE,"E100.MirrorCS"),sQuery(id+"F6.wireOp",EDGE,"E101.MirrorCS"),sQuery(id+"F6.wireOp",EDGE,"E102.MirrorCS"),sQuery(id+"F6.wireOp",EDGE,"E103.MirrorCS"),sQuery(id+"F6.wireOp",EDGE,"E104.MirrorCS"),sQuery(id+"F6.wireOp",EDGE,"E105.MirrorCS"),sQuery(id+"F6.wireOp",EDGE,"E106.MirrorCS"),sQuery(id+"F6.wireOp",EDGE,"E107.MirrorCS")])],"isStart":true})]});}
            var sketch = newSketch(context, id + "F10", { "sketchPlane" : qUnion([Q0])});
            skEllipse(sketch, "E113", {"center": v(-9.48, 12.1) * mm, "majorRadius": 5.03 * mm, "minorRadius": 2.53 * mm, "majorAxis": v(0, -1)});
            skEllipse(sketch, "E114.MirrorC", {"center": v(9.48, 12.1) * mm, "majorRadius": 5.03 * mm, "minorRadius": 2.53 * mm, "majorAxis": v(0, -1)});
            skSolve(sketch);
        }
        {
            var Q0;
            Q0=qSketchRegion(id+"F10",true);
            extrude(context, id + "F11", {"entities" : qUnion([Q0]), "operationType" : NewBodyOperationType.ADD, "oppositeDirection" : true, "depth" : 4 * mm, "offsetDistance" : 25.4 * mm});
        }
        {
            var Q0;
            {var subQ0=sQuery(id+"F0.wireOp",EDGE,"E12");var subQ1=sQuery(id+"F0.wireOp",EDGE,"E11.1.0");var subQ2=sQuery(id+"F0.wireOp",EDGE,"E2");var subQ3=sQuery(id+"F0.wireOp",EDGE,"E1");var subQ4=sQuery(id+"F0.wireOp",EDGE,"E0");Q0=makeQuery(id+"F11.boolean.opBoolean","MERGE",FACE,{"derivedFrom":[makeQuery(id+"F7.boolean.opBoolean","MERGE",FACE,{"derivedFrom":[makeQuery(id+"F4.boolean.opBoolean","MERGE",FACE,{"derivedFrom":[makeQuery(id+"F1.opExtrude","CAP_FACE",FACE,{"disambiguationData":[OSD([subQ4,subQ3,subQ2,sQuery(id+"F0.wireOp",EDGE,"E3.0"),sQuery(id+"F0.wireOp",EDGE,"E4.0"),sQuery(id+"F0.wireOp",EDGE,"E5.0"),sQuery(id+"F0.wireOp",EDGE,"E7.filletArc"),sQuery(id+"F0.wireOp",EDGE,"E8.filletArc"),sQuery(id+"F0.wireOp",EDGE,"E9.filletArc"),sQuery(id+"F0.wireOp",EDGE,"E10.filletArc"),subQ1,sQuery(id+"F0.wireOp",EDGE,"E11.1.3"),sQuery(id+"F0.wireOp",EDGE,"E11.1.4"),sQuery(id+"F0.wireOp",EDGE,"E11.1.5"),sQuery(id+"F0.wireOp",EDGE,"E11.4.0"),sQuery(id+"F0.wireOp",EDGE,"E11.4.1"),sQuery(id+"F0.wireOp",EDGE,"E11.4.2"),subQ0])],"isStart":false}),makeQuery(id+"F4.opExtrude","CAP_FACE",FACE,{"disambiguationData":[OSD([subQ4,subQ3,subQ2,subQ1,sQuery(id+"F0.wireOp",EDGE,"E11.1.1"),sQuery(id+"F0.wireOp",EDGE,"E11.1.2"),sQuery(id+"F0.wireOp",EDGE,"E11.4.3"),sQuery(id+"F0.wireOp",EDGE,"E11.4.4"),sQuery(id+"F0.wireOp",EDGE,"E11.4.5"),subQ0])],"isStart":false})]}),makeQuery(id+"F7.opExtrude","CAP_FACE",FACE,{"disambiguationData":[OSD([sQuery(id+"F6.wireOp",EDGE,"E74"),sQuery(id+"F6.wireOp",EDGE,"E75"),sQuery(id+"F6.wireOp",EDGE,"E76"),sQuery(id+"F6.wireOp",EDGE,"E79"),sQuery(id+"F6.wireOp",EDGE,"E80"),sQuery(id+"F6.wireOp",EDGE,"E81"),sQuery(id+"F6.wireOp",EDGE,"E82"),sQuery(id+"F6.wireOp",EDGE,"E83"),sQuery(id+"F6.wireOp",EDGE,"E84"),sQuery(id+"F6.wireOp",EDGE,"E85"),sQuery(id+"F6.wireOp",EDGE,"E86"),sQuery(id+"F6.wireOp",EDGE,"E87"),sQuery(id+"F6.wireOp",EDGE,"E88"),sQuery(id+"F6.wireOp",EDGE,"E89"),sQuery(id+"F6.wireOp",EDGE,"E90")])],"isStart":true}),makeQuery(id+"F7.opExtrude","CAP_FACE",FACE,{"disambiguationData":[OSD([sQuery(id+"F6.wireOp",EDGE,"E93.MirrorCS"),sQuery(id+"F6.wireOp",EDGE,"E94.MirrorCS"),sQuery(id+"F6.wireOp",EDGE,"E95.MirrorCS"),sQuery(id+"F6.wireOp",EDGE,"E96.MirrorCS"),sQuery(id+"F6.wireOp",EDGE,"E97.MirrorCS"),sQuery(id+"F6.wireOp",EDGE,"E98.MirrorCS"),sQuery(id+"F6.wireOp",EDGE,"E99.MirrorCS"),sQuery(id+"F6.wireOp",EDGE,"E100.MirrorCS"),sQuery(id+"F6.wireOp",EDGE,"E101.MirrorCS"),sQuery(id+"F6.wireOp",EDGE,"E102.MirrorCS"),sQuery(id+"F6.wireOp",EDGE,"E103.MirrorCS"),sQuery(id+"F6.wireOp",EDGE,"E104.MirrorCS"),sQuery(id+"F6.wireOp",EDGE,"E105.MirrorCS"),sQuery(id+"F6.wireOp",EDGE,"E106.MirrorCS"),sQuery(id+"F6.wireOp",EDGE,"E107.MirrorCS")])],"isStart":true})]}),makeQuery(id+"F11.opExtrude","CAP_FACE",FACE,{"disambiguationData":[OSD([sQuery(id+"F10.wireOp",EDGE,"E113")])],"isStart":true}),makeQuery(id+"F11.opExtrude","CAP_FACE",FACE,{"disambiguationData":[OSD([sQuery(id+"F10.wireOp",EDGE,"E114.MirrorC")])],"isStart":true})]});}
            var sketch = newSketch(context, id + "F12", { "sketchPlane" : qUnion([Q0])});
            skLineSegment(sketch, "E115", {"start": v(-12.14, -16.06) * mm, "end": v(-9.04, -18) * mm});
            skLineSegment(sketch, "E116", {"start": v(-9.04, -18) * mm, "end": v(-9.83, -16.7) * mm});
            skLineSegment(sketch, "E117", {"start": v(-9.83, -16.7) * mm, "end": v(-11.71, -15.78) * mm});
            skLineSegment(sketch, "E118", {"start": v(-11.71, -15.78) * mm, "end": v(-12.14, -16.06) * mm});
            skLineSegment(sketch, "E119.MirrorCS", {"start": v(12.14, -16.06) * mm, "end": v(9.04, -18) * mm});
            skLineSegment(sketch, "E120.MirrorCS", {"start": v(9.04, -18) * mm, "end": v(9.83, -16.7) * mm});
            skLineSegment(sketch, "E121.MirrorCS", {"start": v(9.83, -16.7) * mm, "end": v(11.71, -15.78) * mm});
            skLineSegment(sketch, "E122.MirrorCS", {"start": v(11.71, -15.78) * mm, "end": v(12.14, -16.06) * mm});
            skSolve(sketch);
        }
        {
            var Q0;
            Q0=qSketchRegion(id+"F12",true);
            var Q1;
            {var subQ72=sQuery(id+"F12.wireOp",EDGE,"E116");Q1=makeQuery(id+"F12.imprint","IMPRINT",FACE,{"disambiguationData":[TD([[makeQuery(id+"F12.imprint","IMPRINT",EDGE,{"derivedFrom":subQ72}),-1.0]])]});}
            extrude(context, id + "F13", {"entities" : qUnion([Q0, Q1]), "operationType" : NewBodyOperationType.ADD, "oppositeDirection" : true, "depth" : 4 * mm, "offsetDistance" : 25.4 * mm});
        }
        {
            var Q0;
            {var subQ0=sQuery(id+"F0.wireOp",EDGE,"E12");var subQ1=sQuery(id+"F0.wireOp",EDGE,"E11.1.0");var subQ2=sQuery(id+"F0.wireOp",EDGE,"E2");var subQ3=sQuery(id+"F0.wireOp",EDGE,"E1");var subQ4=sQuery(id+"F0.wireOp",EDGE,"E0");Q0=makeQuery(id+"F13.boolean.opBoolean","MERGE",FACE,{"derivedFrom":[makeQuery(id+"F11.boolean.opBoolean","MERGE",FACE,{"derivedFrom":[makeQuery(id+"F7.boolean.opBoolean","MERGE",FACE,{"derivedFrom":[makeQuery(id+"F4.boolean.opBoolean","MERGE",FACE,{"derivedFrom":[makeQuery(id+"F1.opExtrude","CAP_FACE",FACE,{"disambiguationData":[OSD([subQ4,subQ3,subQ2,sQuery(id+"F0.wireOp",EDGE,"E3.0"),sQuery(id+"F0.wireOp",EDGE,"E4.0"),sQuery(id+"F0.wireOp",EDGE,"E5.0"),sQuery(id+"F0.wireOp",EDGE,"E7.filletArc"),sQuery(id+"F0.wireOp",EDGE,"E8.filletArc"),sQuery(id+"F0.wireOp",EDGE,"E9.filletArc"),sQuery(id+"F0.wireOp",EDGE,"E10.filletArc"),subQ1,sQuery(id+"F0.wireOp",EDGE,"E11.1.3"),sQuery(id+"F0.wireOp",EDGE,"E11.1.4"),sQuery(id+"F0.wireOp",EDGE,"E11.1.5"),sQuery(id+"F0.wireOp",EDGE,"E11.4.0"),sQuery(id+"F0.wireOp",EDGE,"E11.4.1"),sQuery(id+"F0.wireOp",EDGE,"E11.4.2"),subQ0])],"isStart":false}),makeQuery(id+"F4.opExtrude","CAP_FACE",FACE,{"disambiguationData":[OSD([subQ4,subQ3,subQ2,subQ1,sQuery(id+"F0.wireOp",EDGE,"E11.1.1"),sQuery(id+"F0.wireOp",EDGE,"E11.1.2"),sQuery(id+"F0.wireOp",EDGE,"E11.4.3"),sQuery(id+"F0.wireOp",EDGE,"E11.4.4"),sQuery(id+"F0.wireOp",EDGE,"E11.4.5"),subQ0])],"isStart":false})]}),makeQuery(id+"F7.opExtrude","CAP_FACE",FACE,{"disambiguationData":[OSD([sQuery(id+"F6.wireOp",EDGE,"E74"),sQuery(id+"F6.wireOp",EDGE,"E75"),sQuery(id+"F6.wireOp",EDGE,"E76"),sQuery(id+"F6.wireOp",EDGE,"E79"),sQuery(id+"F6.wireOp",EDGE,"E80"),sQuery(id+"F6.wireOp",EDGE,"E81"),sQuery(id+"F6.wireOp",EDGE,"E82"),sQuery(id+"F6.wireOp",EDGE,"E83"),sQuery(id+"F6.wireOp",EDGE,"E84"),sQuery(id+"F6.wireOp",EDGE,"E85"),sQuery(id+"F6.wireOp",EDGE,"E86"),sQuery(id+"F6.wireOp",EDGE,"E87"),sQuery(id+"F6.wireOp",EDGE,"E88"),sQuery(id+"F6.wireOp",EDGE,"E89"),sQuery(id+"F6.wireOp",EDGE,"E90")])],"isStart":true}),makeQuery(id+"F7.opExtrude","CAP_FACE",FACE,{"disambiguationData":[OSD([sQuery(id+"F6.wireOp",EDGE,"E93.MirrorCS"),sQuery(id+"F6.wireOp",EDGE,"E94.MirrorCS"),sQuery(id+"F6.wireOp",EDGE,"E95.MirrorCS"),sQuery(id+"F6.wireOp",EDGE,"E96.MirrorCS"),sQuery(id+"F6.wireOp",EDGE,"E97.MirrorCS"),sQuery(id+"F6.wireOp",EDGE,"E98.MirrorCS"),sQuery(id+"F6.wireOp",EDGE,"E99.MirrorCS"),sQuery(id+"F6.wireOp",EDGE,"E100.MirrorCS"),sQuery(id+"F6.wireOp",EDGE,"E101.MirrorCS"),sQuery(id+"F6.wireOp",EDGE,"E102.MirrorCS"),sQuery(id+"F6.wireOp",EDGE,"E103.MirrorCS"),sQuery(id+"F6.wireOp",EDGE,"E104.MirrorCS"),sQuery(id+"F6.wireOp",EDGE,"E105.MirrorCS"),sQuery(id+"F6.wireOp",EDGE,"E106.MirrorCS"),sQuery(id+"F6.wireOp",EDGE,"E107.MirrorCS")])],"isStart":true})]}),makeQuery(id+"F11.opExtrude","CAP_FACE",FACE,{"disambiguationData":[OSD([sQuery(id+"F10.wireOp",EDGE,"E113")])],"isStart":true}),makeQuery(id+"F11.opExtrude","CAP_FACE",FACE,{"disambiguationData":[OSD([sQuery(id+"F10.wireOp",EDGE,"E114.MirrorC")])],"isStart":true})]}),makeQuery(id+"F13.opExtrude","CAP_FACE",FACE,{"disambiguationData":[OSD([sQuery(id+"F12.wireOp",EDGE,"E115"),sQuery(id+"F12.wireOp",EDGE,"E116"),sQuery(id+"F12.wireOp",EDGE,"E117"),sQuery(id+"F12.wireOp",EDGE,"E118")])],"isStart":true}),makeQuery(id+"F13.opExtrude","CAP_FACE",FACE,{"disambiguationData":[OSD([sQuery(id+"F12.wireOp",EDGE,"E119.MirrorCS"),sQuery(id+"F12.wireOp",EDGE,"E120.MirrorCS"),sQuery(id+"F12.wireOp",EDGE,"E121.MirrorCS"),sQuery(id+"F12.wireOp",EDGE,"E122.MirrorCS")])],"isStart":true})]});}
            var sketch = newSketch(context, id + "F14", { "sketchPlane" : qUnion([Q0])});
            skCircle(sketch, "E123", {"center": v(0, 0) * mm, "radius": 10.97 * mm});
            skSolve(sketch);
        }
        {
            var Q0;
            Q0=qSketchRegion(id+"F14",true);
            extrude(context, id + "F15", {"entities" : qUnion([Q0]), "operationType" : NewBodyOperationType.ADD, "oppositeDirection" : true, "depth" : 4 * mm, "offsetDistance" : 25 * mm});
        }
        {
            var Q0;
            Q0=qSketchRegion(id+"F14",true);
            extrude(context, id + "F16", {"entities" : qUnion([Q0]), "operationType" : NewBodyOperationType.ADD, "depth" : 2 * mm, "offsetDistance" : 25 * mm});
        }
        {
            var Q0;
            Q0=makeQuery(id+"F16.opExtrude","CAP_FACE",FACE,{"disambiguationData":[OSD([sQuery(id+"F14.wireOp",EDGE,"E123")])],"isStart":false});
            var sketch = newSketch(context, id + "F17", { "sketchPlane" : qUnion([Q0])});
            skCircle(sketch, "E124", {"center": v(0, 0) * mm, "radius": 6 * mm});
            skCircle(sketch, "E125", {"center": v(0, 0) * mm, "radius": 7.97 * mm});
            skSolve(sketch);
        }
        {
            var Q0;
            Q0=makeQuery(id+"F17.imprint","IMPRINT",FACE,{"disambiguationData":[TD([[makeQuery(id+"F17.imprint","IMPRINT",EDGE,{"derivedFrom":sQuery(id+"F17.wireOp",EDGE,"E124")}),-1.0]])]});
            var Q1;
            Q1=makeQuery(id+"F17.imprint","IMPRINT",FACE,{"disambiguationData":[TD([[makeQuery(id+"F17.imprint","IMPRINT",EDGE,{"derivedFrom":sQuery(id+"F17.wireOp",EDGE,"E124")}),1.0]])]});
            extrude(context, id + "F18", {"entities" : qUnion([Q0, Q1]), "operationType" : NewBodyOperationType.REMOVE, "oppositeDirection" : true, "depth" : 5 * mm, "offsetDistance" : 25 * mm});
        }
        {
            var Q0;
            Q0=makeQuery(id+"F17.imprint","IMPRINT",FACE,{"disambiguationData":[TD([[makeQuery(id+"F17.imprint","IMPRINT",EDGE,{"derivedFrom":sQuery(id+"F17.wireOp",EDGE,"E124")}),1.0]])]});
            extrude(context, id + "F19", {"entities" : qUnion([Q0]), "operationType" : NewBodyOperationType.REMOVE, "oppositeDirection" : true, "depth" : 25 * mm, "offsetDistance" : 25 * mm});
        }
        {
            var Q0;
            Q0=qSketchRegion(id+"F9",true);
            var Q1;
            Q1=sQuery(id+"F9.wireOp",EDGE,"E112");
            revolve(context, id + "F20", {"operationType" : NewBodyOperationType.REMOVE, "surfaceOperationType" : NewSurfaceOperationType.NEW, "entities" : qUnion([Q0]), "axis" : qUnion([Q1]), "revolveType" : RevolveType.FULL, "oppositeDirection" : true});
        }
    });
